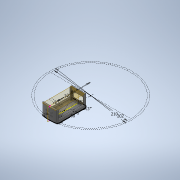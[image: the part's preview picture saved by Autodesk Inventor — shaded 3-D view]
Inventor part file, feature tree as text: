
AUTODESK INVENTOR PART (.ipt)
format: ipt  version: 2020 (Build 240168000, 168)  size: 329,728 bytes
history: native  units: mm
features: projected_geometry x19, extrude x8, sketch x7, other x5
ambient origin geometry x8: Origin, YZ Plane, XZ Plane, XY Plane, X Axis, Y Axis, Z Axis, Center Point
bodies: Body1 (feature_tree)
feature tree (39):
  other  "Твердое тело1"
  sketch  "Эскиз1"
  extrude  "Выдавливание3"  Depth=202.0mm
  other  "РабПлоскость1"
  extrude  "Выдавливание1"  Depth=35.0mm
  other  "РабПлоскость2"
  sketch  "Эскиз2"
  extrude  "Выдавливание4"  Depth=68.0mm
  extrude  "Выдавливание5"  Depth=2.0mm
  sketch  "Эскиз4"
  extrude  "Выдавливание6"  Depth=2.0mm
  extrude  "Выдавливание7"  Depth=3.0mm
  other  "РабПлоскость3"
  extrude  "Выдавливание8"  Depth=3.0mm
  other  "РабПлоскость4"
  extrude  "Выдавливание9"  Depth=210.0mm
  projected_geometry  "Спроецированная петля1"
  projected_geometry  "Спроецированная петля7"
  projected_geometry  "Спроецированная петля8"
  sketch  "Эскиз3"
  projected_geometry  "Спроецированная петля9"
  projected_geometry  "Спроецированная петля10"
  projected_geometry  "Спроецированная петля11"
  projected_geometry  "Спроецированная петля12"
  sketch  "Эскиз5"
  projected_geometry  "Спроецированная петля13"
  projected_geometry  "Спроецированная петля14"
  projected_geometry  "Спроецированная петля15"
  projected_geometry  "Спроецированная петля16"
  projected_geometry  "Спроецированная петля17"
  sketch  "Эскиз6"
  sketch  "Эскиз7"
  projected_geometry  "Спроецированная петля18"
  projected_geometry  "Спроецированная петля19"
  projected_geometry  "Спроецированная петля20"
  projected_geometry  "Спроецированная петля21"
  projected_geometry  "Спроецированная петля22"
  projected_geometry  "Спроецированная петля23"
  projected_geometry  "Спроецированная петля24"
